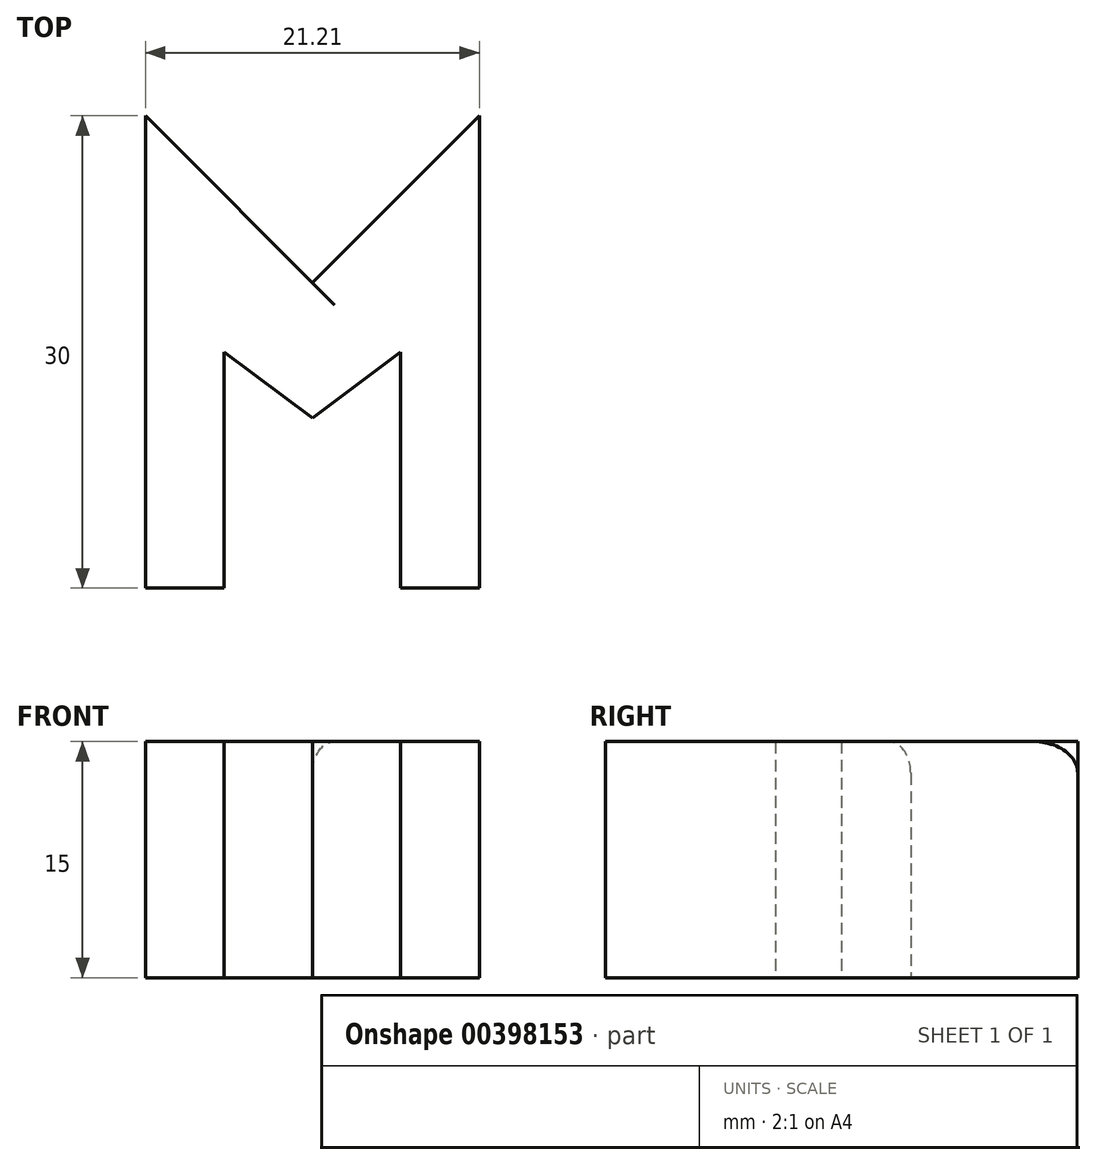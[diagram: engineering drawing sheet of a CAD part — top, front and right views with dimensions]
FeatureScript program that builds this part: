
annotation { "Feature Type Name" : "Feature", "Feature Type Description" : "" }
export const myFeature = defineFeature(function(context is Context, id is Id, definition is map)
    precondition{}
    {
        {
            var Q0;
            Q0=qCreatedBy(makeId("Top.planeOp"),FACE);
            var sketch = newSketch(context, id + "F0", { "sketchPlane" : qUnion([Q0])});
            skLineSegment(sketch, "E0", {"start": v(0, 0) * mm, "end": v(0, 30) * mm});
            skLineSegment(sketch, "E1", {"start": v(0, 30) * mm, "end": v(10.6, 19.4) * mm});
            skLineSegment(sketch, "E2", {"start": v(10.6, 19.4) * mm, "end": v(21.21, 30) * mm});
            skLineSegment(sketch, "E3", {"start": v(21.21, 30) * mm, "end": v(21.21, 0) * mm});
            skLineSegment(sketch, "E4", {"start": v(0, 0) * mm, "end": v(5, 0) * mm});
            skLineSegment(sketch, "E5", {"start": v(21.21, 0) * mm, "end": v(16.21, 0) * mm});
            skLineSegment(sketch, "E6", {"start": v(5, 0) * mm, "end": v(5, 15) * mm});
            skPoint(sketch, "E6.endSnap0", {"position": v(21.21, 15) * mm});
            skLineSegment(sketch, "E7", {"start": v(16.21, 0) * mm, "end": v(16.21, 15) * mm});
            skPoint(sketch, "E7.endSnap0", {"position": v(0, 15) * mm});
            skLineSegment(sketch, "E8", {"start": v(5, 15) * mm, "end": v(10.6, 10.8) * mm});
            skLineSegment(sketch, "E9", {"start": v(10.6, 10.8) * mm, "end": v(16.21, 15) * mm});
            skSolve(sketch);
        }
        {
            var Q0;
            Q0 = qSketchRegion(id + "F0", true);
            extrude(context, id + "F1", {"entities" : qUnion([Q0]), "depth" : 15 * mm});
        }
        {
            var Q0;
            Q0=makeQuery(id+"F1.opExtrude","CAP_EDGE",EDGE,{"disambiguationData":[OSD([sQuery(id+"F0.wireOp",EDGE,"E2")])],"isStart":false});
            fillet(context, id + "F2", {"entities" : qUnion([Q0]), "radius" : 2 * mm, "tangentPropagation" : true, "allowEdgeOverflow" : false});
        }
    });
